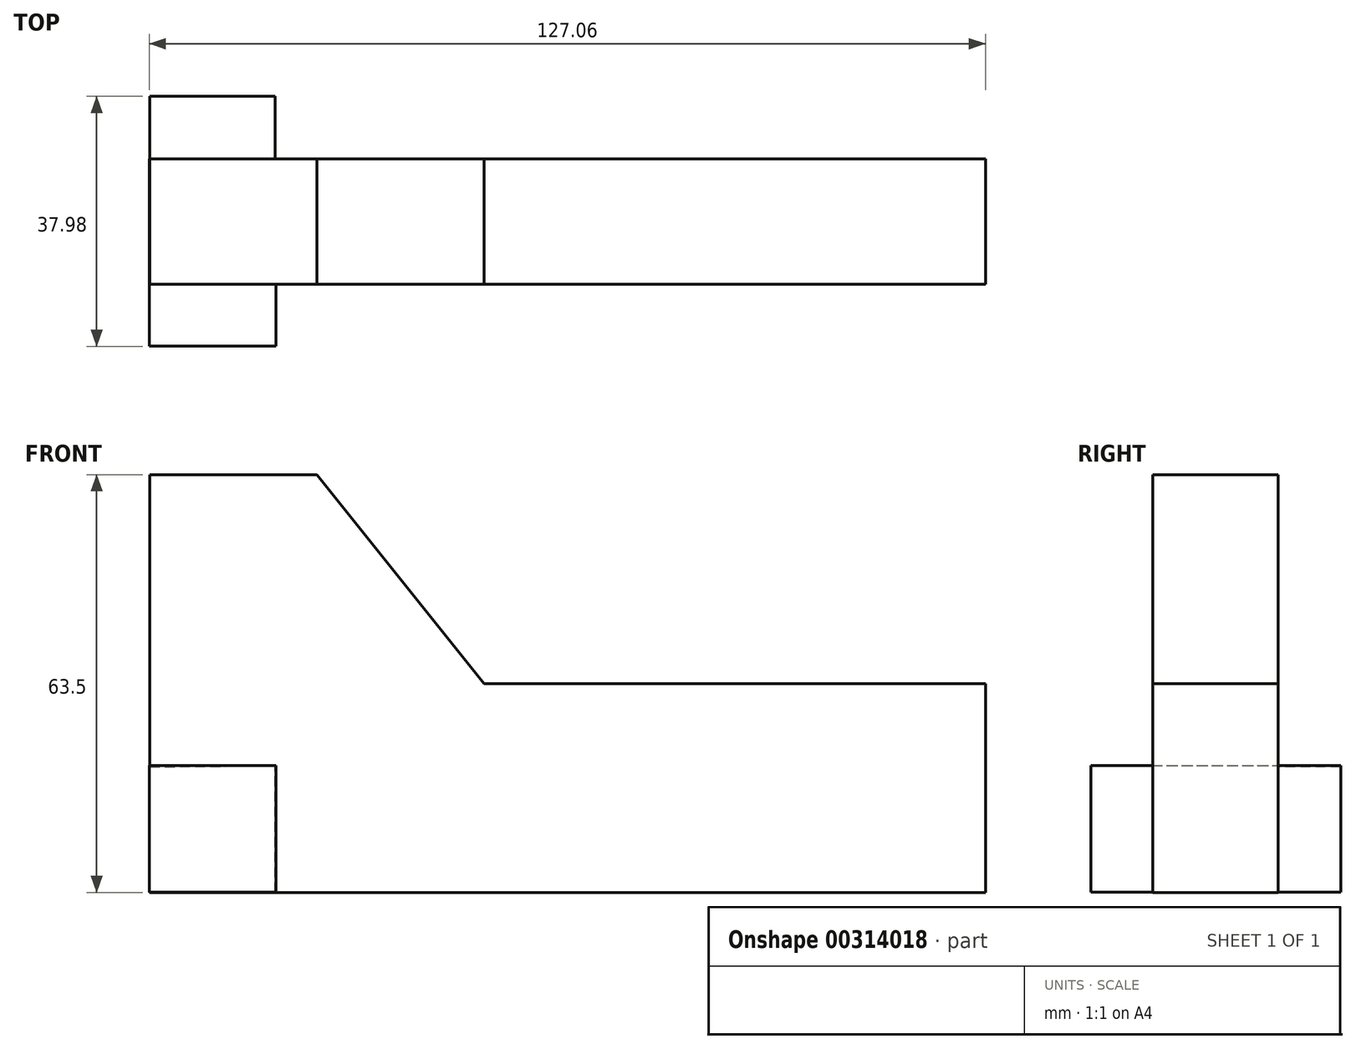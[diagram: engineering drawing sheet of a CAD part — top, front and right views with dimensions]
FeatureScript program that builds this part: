
annotation { "Feature Type Name" : "Feature", "Feature Type Description" : "" }
export const myFeature = defineFeature(function(context is Context, id is Id, definition is map)
    precondition{}
    {
        {
            var Q0;
            Q0=qCreatedBy(makeId("Front.planeOp"),FACE);
            var sketch = newSketch(context, id + "F0", { "sketchPlane" : qUnion([Q0])});
            skLineSegment(sketch, "E0", {"start": v(-49.93, 34.2) * mm, "end": v(-24.53, 34.2) * mm});
            skLineSegment(sketch, "E1", {"start": v(-49.93, -29.3) * mm, "end": v(77.07, -29.3) * mm});
            skLineSegment(sketch, "E2", {"start": v(-49.93, 34.2) * mm, "end": v(-49.93, -29.3) * mm});
            skLineSegment(sketch, "E3", {"start": v(77.07, -29.3) * mm, "end": v(77.07, 2.44) * mm});
            skLineSegment(sketch, "E4", {"start": v(77.07, 2.44) * mm, "end": v(0.87, 2.44) * mm});
            skLineSegment(sketch, "E5", {"start": v(-24.53, 34.2) * mm, "end": v(0.87, 2.44) * mm});
            skSolve(sketch);
        }
        {
            var Q0;
            Q0 = qSketchRegion(id + "F0", true);
            extrude(context, id + "F1", {"entities" : qUnion([Q0]), "depth" : 19.05 * mm});
        }
        {
            var Q0;
            Q0=qCreatedBy(makeId("Front.planeOp"),FACE);
            var sketch = newSketch(context, id + "F2", { "sketchPlane" : qUnion([Q0])});
            skLineSegment(sketch, "E6", {"start": v(-49.9, -29.3) * mm, "end": v(-30.85, -29.3) * mm});
            skLineSegment(sketch, "E7", {"start": v(-49.9, -29.3) * mm, "end": v(-49.9, -10.24) * mm});
            skLineSegment(sketch, "E8", {"start": v(-30.85, -29.3) * mm, "end": v(-30.85, -10.06) * mm});
            skLineSegment(sketch, "E9", {"start": v(-49.9, -10.24) * mm, "end": v(-30.85, -10.06) * mm});
            skSolve(sketch);
        }
        {
            var Q0;
            Q0=makeQuery(id+"F2.imprint","IMPRINT",FACE,{"disambiguationData":[TD([[makeQuery(id+"F2.imprint","IMPRINT",EDGE,{"derivedFrom":sQuery(id+"F2.wireOp",EDGE,"E6")}),1.0]])]});
            extrude(context, id + "F3", {"entities" : qUnion([Q0]), "operationType" : NewBodyOperationType.ADD, "oppositeDirection" : true, "depth" : 9.52 * mm});
        }
        {
            var Q0;
            Q0=qCreatedBy(makeId("Front.planeOp"),FACE);
            var sketch = newSketch(context, id + "F4", { "sketchPlane" : qUnion([Q0])});
            skLineSegment(sketch, "E10", {"start": v(-49.99, -29.3) * mm, "end": v(-30.75, -29.3) * mm});
            skLineSegment(sketch, "E11", {"start": v(-30.75, -29.3) * mm, "end": v(-30.75, -10.06) * mm});
            skLineSegment(sketch, "E12", {"start": v(-30.75, -10.06) * mm, "end": v(-49.99, -10.06) * mm});
            skLineSegment(sketch, "E13", {"start": v(-49.99, -10.06) * mm, "end": v(-49.99, -29.3) * mm});
            skSolve(sketch);
        }
        {
            var Q0;
            Q0 = qSketchRegion(id + "F4", true);
            extrude(context, id + "F5", {"entities" : qUnion([Q0]), "operationType" : NewBodyOperationType.ADD, "depth" : 28.45 * mm});
        }
    });
